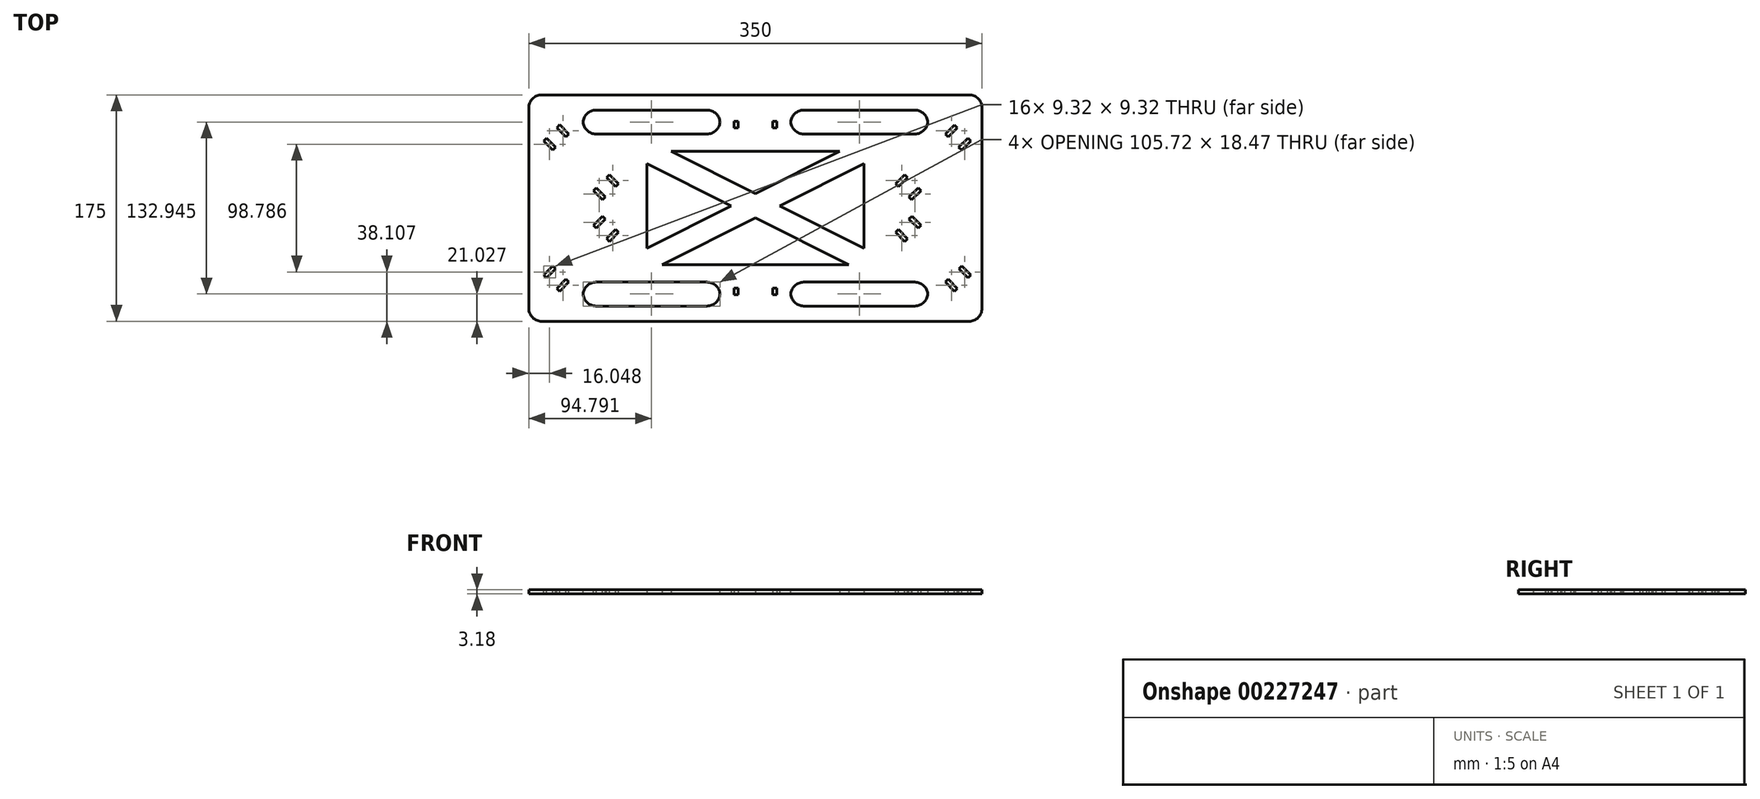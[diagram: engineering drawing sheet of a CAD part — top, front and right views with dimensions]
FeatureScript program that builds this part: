
annotation { "Feature Type Name" : "Feature", "Feature Type Description" : "" }
export const myFeature = defineFeature(function(context is Context, id is Id, definition is map)
    precondition{}
    {
        {
            var Q0;
            Q0=qCreatedBy(makeId("Top.planeOp"),FACE);
            var sketch = newSketch(context, id + "F0", { "sketchPlane" : qUnion([Q0])});
            skLineSegment(sketch, "E0.bottom", {"start": v(175, -87.5) * mm, "end": v(-175, -87.5) * mm});
            skLineSegment(sketch, "E0.top", {"start": v(175, 87.5) * mm, "end": v(-175, 87.5) * mm});
            skLineSegment(sketch, "E0.left", {"start": v(175, -87.5) * mm, "end": v(175, 87.5) * mm});
            skLineSegment(sketch, "E0.right", {"start": v(-175, -87.5) * mm, "end": v(-175, 87.5) * mm});
            skPoint(sketch, "E0.middle", {"position": v(0, 0) * mm});
            skLineSegment(sketch, "E1.bottom", {"start": v(-13.41, 62) * mm, "end": v(-16.59, 62) * mm});
            skLineSegment(sketch, "E1.top", {"start": v(-13.41, 67) * mm, "end": v(-16.59, 67) * mm});
            skLineSegment(sketch, "E1.left", {"start": v(-13.41, 62) * mm, "end": v(-13.41, 67) * mm});
            skLineSegment(sketch, "E1.right", {"start": v(-16.59, 62) * mm, "end": v(-16.59, 67) * mm});
            skPoint(sketch, "E1.middle", {"position": v(-15, 64.5) * mm});
            skLineSegment(sketch, "E2.bottom", {"start": v(13.41, 67) * mm, "end": v(16.59, 67) * mm});
            skLineSegment(sketch, "E2.top", {"start": v(13.41, 62) * mm, "end": v(16.59, 62) * mm});
            skLineSegment(sketch, "E2.left", {"start": v(13.41, 67) * mm, "end": v(13.41, 62) * mm});
            skLineSegment(sketch, "E2.right", {"start": v(16.59, 67) * mm, "end": v(16.59, 62) * mm});
            skPoint(sketch, "E3.0.1.0", {"position": v(-15, -64.5) * mm});
            skLineSegment(sketch, "E3.0.1.1", {"start": v(-16.59, -67) * mm, "end": v(-16.59, -62) * mm});
            skLineSegment(sketch, "E3.0.1.2", {"start": v(13.41, -62) * mm, "end": v(13.41, -67) * mm});
            skLineSegment(sketch, "E3.0.1.3", {"start": v(-13.41, -62) * mm, "end": v(-16.59, -62) * mm});
            skLineSegment(sketch, "E3.0.1.4", {"start": v(13.41, -67) * mm, "end": v(16.59, -67) * mm});
            skLineSegment(sketch, "E3.0.1.5", {"start": v(-13.41, -67) * mm, "end": v(-16.59, -67) * mm});
            skLineSegment(sketch, "E3.0.1.6", {"start": v(13.41, -62) * mm, "end": v(16.59, -62) * mm});
            skLineSegment(sketch, "E3.0.1.7", {"start": v(16.59, -62) * mm, "end": v(16.59, -67) * mm});
            skLineSegment(sketch, "E3.0.1.8", {"start": v(-13.41, -67) * mm, "end": v(-13.41, -62) * mm});
            skLineSegment(sketch, "E3.direction1", {"start": v(-16.59, 62) * mm, "end": v(8.41, 62) * mm, "construction": true});
            skLineSegment(sketch, "E3.direction2", {"start": v(-16.59, 62) * mm, "end": v(-16.59, -67) * mm, "construction": true});
            skSolve(sketch);
        }
        {
            var Q0;
            Q0 = qSketchRegion(id + "F0", true);
            extrude(context, id + "F1", {"entities" : qUnion([Q0]), "depth" : 3.17 * mm});
        }
        {
            var Q0;
            Q0=makeQuery(id+"F1.opExtrude","CAP_FACE",FACE,{"disambiguationData":[OSD([sQuery(id+"F0.wireOp",EDGE,"E0.bottom"),sQuery(id+"F0.wireOp",EDGE,"E0.top"),sQuery(id+"F0.wireOp",EDGE,"E0.left"),sQuery(id+"F0.wireOp",EDGE,"E0.right"),sQuery(id+"F0.wireOp",EDGE,"E1.bottom"),sQuery(id+"F0.wireOp",EDGE,"E1.top"),sQuery(id+"F0.wireOp",EDGE,"E1.left"),sQuery(id+"F0.wireOp",EDGE,"E1.right"),sQuery(id+"F0.wireOp",EDGE,"E2.bottom"),sQuery(id+"F0.wireOp",EDGE,"E2.top"),sQuery(id+"F0.wireOp",EDGE,"E2.left"),sQuery(id+"F0.wireOp",EDGE,"E2.right"),sQuery(id+"F0.wireOp",EDGE,"E3.0.1.1"),sQuery(id+"F0.wireOp",EDGE,"E3.0.1.2"),sQuery(id+"F0.wireOp",EDGE,"E3.0.1.3"),sQuery(id+"F0.wireOp",EDGE,"E3.0.1.4"),sQuery(id+"F0.wireOp",EDGE,"E3.0.1.5"),sQuery(id+"F0.wireOp",EDGE,"E3.0.1.6"),sQuery(id+"F0.wireOp",EDGE,"E3.0.1.7"),sQuery(id+"F0.wireOp",EDGE,"E3.0.1.8")])],"isStart":false});
            var sketch = newSketch(context, id + "F2", { "sketchPlane" : qUnion([Q0])});
            skLineSegment(sketch, "E4", {"start": v(-163.61, -51.8) * mm, "end": v(-156.54, -44.74) * mm});
            skLineSegment(sketch, "E5", {"start": v(-156.54, -44.74) * mm, "end": v(-154.3, -46.98) * mm});
            skLineSegment(sketch, "E6", {"start": v(-154.3, -46.98) * mm, "end": v(-161.36, -54.05) * mm});
            skLineSegment(sketch, "E7", {"start": v(-161.36, -54.05) * mm, "end": v(-163.61, -51.8) * mm});
            skLineSegment(sketch, "E8", {"start": v(-153.35, -62.06) * mm, "end": v(-146.28, -55) * mm});
            skLineSegment(sketch, "E9", {"start": v(-146.28, -55) * mm, "end": v(-144.04, -57.24) * mm});
            skLineSegment(sketch, "E10", {"start": v(-144.04, -57.24) * mm, "end": v(-151.1, -64.3) * mm});
            skLineSegment(sketch, "E11", {"start": v(-151.1, -64.3) * mm, "end": v(-153.35, -62.06) * mm});
            skLineSegment(sketch, "E12", {"start": v(166.32, 51.8) * mm, "end": v(164.07, 54.05) * mm});
            skLineSegment(sketch, "E13", {"start": v(164.07, 54.05) * mm, "end": v(157, 46.98) * mm});
            skLineSegment(sketch, "E14", {"start": v(157, 46.98) * mm, "end": v(159.24, 44.74) * mm});
            skLineSegment(sketch, "E15", {"start": v(159.24, 44.74) * mm, "end": v(166.32, 51.8) * mm});
            skLineSegment(sketch, "E16", {"start": v(156.06, 62.06) * mm, "end": v(153.81, 64.3) * mm});
            skLineSegment(sketch, "E17", {"start": v(153.81, 64.3) * mm, "end": v(146.74, 57.24) * mm});
            skLineSegment(sketch, "E18", {"start": v(146.74, 57.24) * mm, "end": v(148.99, 55) * mm});
            skLineSegment(sketch, "E19", {"start": v(148.99, 55) * mm, "end": v(156.06, 62.06) * mm});
            skLineSegment(sketch, "E20", {"start": v(-163.61, 51.8) * mm, "end": v(-161.36, 54.05) * mm});
            skLineSegment(sketch, "E21", {"start": v(-161.36, 54.05) * mm, "end": v(-154.3, 46.98) * mm});
            skLineSegment(sketch, "E22", {"start": v(-154.3, 46.98) * mm, "end": v(-156.54, 44.74) * mm});
            skLineSegment(sketch, "E23", {"start": v(-156.54, 44.74) * mm, "end": v(-163.61, 51.8) * mm});
            skLineSegment(sketch, "E24", {"start": v(-153.32, 62.1) * mm, "end": v(-151.07, 64.34) * mm});
            skLineSegment(sketch, "E25", {"start": v(-151.07, 64.34) * mm, "end": v(-144, 57.27) * mm});
            skLineSegment(sketch, "E26", {"start": v(-144, 57.27) * mm, "end": v(-146.25, 55.03) * mm});
            skLineSegment(sketch, "E27", {"start": v(-146.25, 55.03) * mm, "end": v(-153.32, 62.1) * mm});
            skLineSegment(sketch, "E28", {"start": v(164.12, -54.04) * mm, "end": v(166.37, -51.8) * mm});
            skLineSegment(sketch, "E29", {"start": v(166.37, -51.8) * mm, "end": v(159.3, -44.72) * mm});
            skLineSegment(sketch, "E30", {"start": v(159.3, -44.72) * mm, "end": v(157.05, -46.97) * mm});
            skLineSegment(sketch, "E31", {"start": v(157.05, -46.97) * mm, "end": v(164.12, -54.04) * mm});
            skLineSegment(sketch, "E32", {"start": v(153.83, -64.33) * mm, "end": v(156.07, -62.09) * mm});
            skLineSegment(sketch, "E33", {"start": v(156.07, -62.09) * mm, "end": v(149, -55.02) * mm});
            skLineSegment(sketch, "E34", {"start": v(149, -55.02) * mm, "end": v(146.76, -57.26) * mm});
            skLineSegment(sketch, "E35", {"start": v(146.76, -57.26) * mm, "end": v(153.83, -64.33) * mm});
            skLineSegment(sketch, "E36", {"start": v(125.65, -15.57) * mm, "end": v(127.9, -13.33) * mm});
            skLineSegment(sketch, "E37", {"start": v(127.9, -13.33) * mm, "end": v(120.83, -6.26) * mm});
            skLineSegment(sketch, "E38", {"start": v(120.83, -6.26) * mm, "end": v(118.58, -8.5) * mm});
            skLineSegment(sketch, "E39", {"start": v(118.58, -8.5) * mm, "end": v(125.65, -15.57) * mm});
            skLineSegment(sketch, "E40", {"start": v(115.36, -25.86) * mm, "end": v(117.6, -23.62) * mm});
            skLineSegment(sketch, "E41", {"start": v(117.6, -23.62) * mm, "end": v(110.54, -16.55) * mm});
            skLineSegment(sketch, "E42", {"start": v(110.54, -16.55) * mm, "end": v(108.3, -18.8) * mm});
            skLineSegment(sketch, "E43", {"start": v(108.3, -18.8) * mm, "end": v(115.36, -25.86) * mm});
            skLineSegment(sketch, "E44", {"start": v(127.85, 13.34) * mm, "end": v(125.6, 15.58) * mm});
            skLineSegment(sketch, "E45", {"start": v(125.6, 15.58) * mm, "end": v(118.53, 8.51) * mm});
            skLineSegment(sketch, "E46", {"start": v(118.53, 8.51) * mm, "end": v(120.78, 6.27) * mm});
            skLineSegment(sketch, "E47", {"start": v(120.78, 6.27) * mm, "end": v(127.85, 13.34) * mm});
            skLineSegment(sketch, "E48", {"start": v(117.6, 23.6) * mm, "end": v(115.35, 25.84) * mm});
            skLineSegment(sketch, "E49", {"start": v(115.35, 25.84) * mm, "end": v(108.28, 18.77) * mm});
            skLineSegment(sketch, "E50", {"start": v(108.28, 18.77) * mm, "end": v(110.52, 16.52) * mm});
            skLineSegment(sketch, "E51", {"start": v(110.52, 16.52) * mm, "end": v(117.6, 23.6) * mm});
            skLineSegment(sketch, "E52", {"start": v(-125.14, 13.34) * mm, "end": v(-122.9, 15.58) * mm});
            skLineSegment(sketch, "E53", {"start": v(-122.9, 15.58) * mm, "end": v(-115.83, 8.51) * mm});
            skLineSegment(sketch, "E54", {"start": v(-115.83, 8.51) * mm, "end": v(-118.07, 6.27) * mm});
            skLineSegment(sketch, "E55", {"start": v(-118.07, 6.27) * mm, "end": v(-125.14, 13.34) * mm});
            skLineSegment(sketch, "E56", {"start": v(-114.85, 23.63) * mm, "end": v(-112.6, 25.88) * mm});
            skLineSegment(sketch, "E57", {"start": v(-112.6, 25.88) * mm, "end": v(-105.54, 18.8) * mm});
            skLineSegment(sketch, "E58", {"start": v(-105.54, 18.8) * mm, "end": v(-107.78, 16.56) * mm});
            skLineSegment(sketch, "E59", {"start": v(-107.78, 16.56) * mm, "end": v(-114.85, 23.63) * mm});
            skLineSegment(sketch, "E60", {"start": v(-125.14, -13.34) * mm, "end": v(-118.07, -6.27) * mm});
            skLineSegment(sketch, "E61", {"start": v(-118.07, -6.27) * mm, "end": v(-115.83, -8.51) * mm});
            skLineSegment(sketch, "E62", {"start": v(-115.83, -8.51) * mm, "end": v(-122.9, -15.58) * mm});
            skLineSegment(sketch, "E63", {"start": v(-122.9, -15.58) * mm, "end": v(-125.14, -13.34) * mm});
            skLineSegment(sketch, "E64", {"start": v(-114.89, -23.6) * mm, "end": v(-107.82, -16.52) * mm});
            skLineSegment(sketch, "E65", {"start": v(-107.82, -16.52) * mm, "end": v(-105.57, -18.77) * mm});
            skLineSegment(sketch, "E66", {"start": v(-105.57, -18.77) * mm, "end": v(-112.64, -25.84) * mm});
            skLineSegment(sketch, "E67", {"start": v(-112.64, -25.84) * mm, "end": v(-114.89, -23.6) * mm});
            skSolve(sketch);
        }
        {
            var Q0;
            Q0 = qSketchRegion(id + "F2", true);
            extrude(context, id + "F3", {"entities" : qUnion([Q0]), "operationType" : NewBodyOperationType.REMOVE, "oppositeDirection" : true, "depth" : 25 * mm});
        }
        {
            var Q0;
            Q0=makeQuery(id+"F1.opExtrude","CAP_FACE",FACE,{"disambiguationData":[OSD([sQuery(id+"F0.wireOp",EDGE,"E0.bottom"),sQuery(id+"F0.wireOp",EDGE,"E0.top"),sQuery(id+"F0.wireOp",EDGE,"E0.left"),sQuery(id+"F0.wireOp",EDGE,"E0.right"),sQuery(id+"F0.wireOp",EDGE,"E1.bottom"),sQuery(id+"F0.wireOp",EDGE,"E1.top"),sQuery(id+"F0.wireOp",EDGE,"E1.left"),sQuery(id+"F0.wireOp",EDGE,"E1.right"),sQuery(id+"F0.wireOp",EDGE,"E2.bottom"),sQuery(id+"F0.wireOp",EDGE,"E2.top"),sQuery(id+"F0.wireOp",EDGE,"E2.left"),sQuery(id+"F0.wireOp",EDGE,"E2.right"),sQuery(id+"F0.wireOp",EDGE,"E3.0.1.1"),sQuery(id+"F0.wireOp",EDGE,"E3.0.1.2"),sQuery(id+"F0.wireOp",EDGE,"E3.0.1.3"),sQuery(id+"F0.wireOp",EDGE,"E3.0.1.4"),sQuery(id+"F0.wireOp",EDGE,"E3.0.1.5"),sQuery(id+"F0.wireOp",EDGE,"E3.0.1.6"),sQuery(id+"F0.wireOp",EDGE,"E3.0.1.7"),sQuery(id+"F0.wireOp",EDGE,"E3.0.1.8")])],"isStart":false});
            var sketch = newSketch(context, id + "F4", { "sketchPlane" : qUnion([Q0])});
            skLineSegment(sketch, "E68.bottom", {"start": v(138.9, -44.1) * mm, "end": v(-138.9, -44.1) * mm});
            skLineSegment(sketch, "E68.top", {"start": v(138.9, 44.1) * mm, "end": v(-138.9, 44.1) * mm});
            skLineSegment(sketch, "E68.left", {"start": v(138.9, -44.1) * mm, "end": v(138.9, 44.1) * mm});
            skLineSegment(sketch, "E68.right", {"start": v(-138.9, -44.1) * mm, "end": v(-138.9, 44.1) * mm});
            skPoint(sketch, "E68.middle", {"position": v(0, 0) * mm});
            skLineSegment(sketch, "E69", {"start": v(-138.9, 33.15) * mm, "end": v(124.66, -44.1) * mm});
            skLineSegment(sketch, "E70", {"start": v(-127.9, 44.1) * mm, "end": v(138.9, -34.1) * mm});
            skLineSegment(sketch, "E71.MirrorCS", {"start": v(127.9, 44.1) * mm, "end": v(-138.9, -34.1) * mm});
            skLineSegment(sketch, "E72.MirrorCS", {"start": v(138.9, 33.15) * mm, "end": v(-124.66, -44.1) * mm});
            skLineSegment(sketch, "E73.bottom", {"start": v(-133.1, -57.24) * mm, "end": v(-27.32, -57.24) * mm});
            skLineSegment(sketch, "E73.top", {"start": v(-133.1, -75.7) * mm, "end": v(-27.32, -75.7) * mm});
            skLineSegment(sketch, "E73.left", {"start": v(-133.1, -57.24) * mm, "end": v(-133.1, -75.7) * mm});
            skLineSegment(sketch, "E73.right", {"start": v(-27.32, -57.24) * mm, "end": v(-27.32, -75.7) * mm});
            skLineSegment(sketch, "E74.MirrorCS", {"start": v(27.32, -57.24) * mm, "end": v(27.32, -75.7) * mm});
            skLineSegment(sketch, "E75.MirrorCS", {"start": v(133.1, -57.24) * mm, "end": v(27.32, -57.24) * mm});
            skLineSegment(sketch, "E76.MirrorCS", {"start": v(133.1, -57.24) * mm, "end": v(133.1, -75.7) * mm});
            skLineSegment(sketch, "E77.MirrorCS", {"start": v(133.1, -75.7) * mm, "end": v(27.32, -75.7) * mm});
            skLineSegment(sketch, "E78.MirrorCS", {"start": v(133.1, 75.7) * mm, "end": v(27.32, 75.7) * mm});
            skLineSegment(sketch, "E79.MirrorCS", {"start": v(-133.1, 57.24) * mm, "end": v(-27.32, 57.24) * mm});
            skLineSegment(sketch, "E80.MirrorCS", {"start": v(-133.1, 75.7) * mm, "end": v(-27.32, 75.7) * mm});
            skLineSegment(sketch, "E81.MirrorCS", {"start": v(-133.1, 57.24) * mm, "end": v(-133.1, 75.7) * mm});
            skLineSegment(sketch, "E82.MirrorCS", {"start": v(-27.32, 57.24) * mm, "end": v(-27.32, 75.7) * mm});
            skLineSegment(sketch, "E83.MirrorCS", {"start": v(133.1, 57.24) * mm, "end": v(27.32, 57.24) * mm});
            skLineSegment(sketch, "E84.MirrorCS", {"start": v(133.1, 57.24) * mm, "end": v(133.1, 75.7) * mm});
            skLineSegment(sketch, "E85.MirrorCS", {"start": v(27.32, 57.24) * mm, "end": v(27.32, 75.7) * mm});
            skSolve(sketch);
        }
        {
            var Q0;
            Q0=makeQuery(id+"F4.imprint","IMPRINT",FACE,{"disambiguationData":[TD([[makeQuery(id+"F4.imprint","IMPRINT",EDGE,{"derivedFrom":sQuery(id+"F4.wireOp",EDGE,"E79.MirrorCS")}),1.0]])]});
            var Q1;
            Q1=makeQuery(id+"F4.imprint","IMPRINT",FACE,{"disambiguationData":[TD([[makeQuery(id+"F4.imprint","IMPRINT",EDGE,{"derivedFrom":sQuery(id+"F4.wireOp",EDGE,"E73.bottom")}),-1.0]])]});
            var Q2;
            Q2=makeQuery(id+"F4.imprint","IMPRINT",FACE,{"disambiguationData":[TD([[makeQuery(id+"F4.imprint","IMPRINT",EDGE,{"derivedFrom":sQuery(id+"F4.wireOp",EDGE,"E74.MirrorCS")}),1.0]])]});
            var Q3;
            Q3=makeQuery(id+"F4.imprint","IMPRINT",FACE,{"disambiguationData":[TD([[makeQuery(id+"F4.imprint","IMPRINT",EDGE,{"derivedFrom":sQuery(id+"F4.wireOp",EDGE,"E78.MirrorCS")}),1.0]])]});
            extrude(context, id + "F5", {"entities" : qUnion([Q0, Q1, Q2, Q3]), "operationType" : NewBodyOperationType.REMOVE, "oppositeDirection" : true, "depth" : 25 * mm});
        }
        {
            var Q0;
            Q0=makeQuery(id+"F1.opExtrude","SWEPT_EDGE",EDGE,{"disambiguationData":[OSD([sQuery(id+"F0.wireOp",EDGE,"E0.top"),sQuery(id+"F0.wireOp",EDGE,"E0.right")])]});
            var Q1;
            Q1=makeQuery(id+"F1.opExtrude","SWEPT_EDGE",EDGE,{"disambiguationData":[OSD([sQuery(id+"F0.wireOp",EDGE,"E0.top"),sQuery(id+"F0.wireOp",EDGE,"E0.left")])]});
            var Q2;
            Q2=makeQuery(id+"F1.opExtrude","SWEPT_EDGE",EDGE,{"disambiguationData":[OSD([sQuery(id+"F0.wireOp",EDGE,"E0.bottom"),sQuery(id+"F0.wireOp",EDGE,"E0.left")])]});
            var Q3;
            Q3=makeQuery(id+"F1.opExtrude","SWEPT_EDGE",EDGE,{"disambiguationData":[OSD([sQuery(id+"F0.wireOp",EDGE,"E0.bottom"),sQuery(id+"F0.wireOp",EDGE,"E0.right")])]});
            var Q4;
            Q4=makeQuery(id+"F5.boolean.opBoolean","COPY",EDGE,{"derivedFrom":makeQuery(id+"F5.opExtrude","SWEPT_EDGE",EDGE,{"disambiguationData":[OSD([sQuery(id+"F4.wireOp",EDGE,"E73.top"),sQuery(id+"F4.wireOp",EDGE,"E73.left")])]})});
            var Q5;
            Q5=makeQuery(id+"F5.boolean.opBoolean","COPY",EDGE,{"derivedFrom":makeQuery(id+"F5.opExtrude","SWEPT_EDGE",EDGE,{"disambiguationData":[OSD([sQuery(id+"F4.wireOp",EDGE,"E73.bottom"),sQuery(id+"F4.wireOp",EDGE,"E73.left")])]})});
            var Q6;
            Q6=makeQuery(id+"F5.boolean.opBoolean","COPY",EDGE,{"derivedFrom":makeQuery(id+"F5.opExtrude","SWEPT_EDGE",EDGE,{"disambiguationData":[OSD([sQuery(id+"F4.wireOp",EDGE,"E73.bottom"),sQuery(id+"F4.wireOp",EDGE,"E73.right")])]})});
            var Q7;
            Q7=makeQuery(id+"F5.boolean.opBoolean","COPY",EDGE,{"derivedFrom":makeQuery(id+"F5.opExtrude","SWEPT_EDGE",EDGE,{"disambiguationData":[OSD([sQuery(id+"F4.wireOp",EDGE,"E73.top"),sQuery(id+"F4.wireOp",EDGE,"E73.right")])]})});
            var Q8;
            Q8=makeQuery(id+"F5.boolean.opBoolean","COPY",EDGE,{"derivedFrom":makeQuery(id+"F5.opExtrude","SWEPT_EDGE",EDGE,{"disambiguationData":[OSD([sQuery(id+"F4.wireOp",EDGE,"E75.MirrorCS"),sQuery(id+"F4.wireOp",EDGE,"E76.MirrorCS")])]})});
            var Q9;
            Q9=makeQuery(id+"F5.boolean.opBoolean","COPY",EDGE,{"derivedFrom":makeQuery(id+"F5.opExtrude","SWEPT_EDGE",EDGE,{"disambiguationData":[OSD([sQuery(id+"F4.wireOp",EDGE,"E76.MirrorCS"),sQuery(id+"F4.wireOp",EDGE,"E77.MirrorCS")])]})});
            var Q10;
            Q10=makeQuery(id+"F5.boolean.opBoolean","COPY",EDGE,{"derivedFrom":makeQuery(id+"F5.opExtrude","SWEPT_EDGE",EDGE,{"disambiguationData":[OSD([sQuery(id+"F4.wireOp",EDGE,"E74.MirrorCS"),sQuery(id+"F4.wireOp",EDGE,"E75.MirrorCS")])]})});
            var Q11;
            Q11=makeQuery(id+"F5.boolean.opBoolean","COPY",EDGE,{"derivedFrom":makeQuery(id+"F5.opExtrude","SWEPT_EDGE",EDGE,{"disambiguationData":[OSD([sQuery(id+"F4.wireOp",EDGE,"E74.MirrorCS"),sQuery(id+"F4.wireOp",EDGE,"E77.MirrorCS")])]})});
            var Q12;
            Q12=makeQuery(id+"F5.boolean.opBoolean","COPY",EDGE,{"derivedFrom":makeQuery(id+"F5.opExtrude","SWEPT_EDGE",EDGE,{"disambiguationData":[OSD([sQuery(id+"F4.wireOp",EDGE,"E78.MirrorCS"),sQuery(id+"F4.wireOp",EDGE,"E84.MirrorCS")])]})});
            var Q13;
            Q13=makeQuery(id+"F5.boolean.opBoolean","COPY",EDGE,{"derivedFrom":makeQuery(id+"F5.opExtrude","SWEPT_EDGE",EDGE,{"disambiguationData":[OSD([sQuery(id+"F4.wireOp",EDGE,"E83.MirrorCS"),sQuery(id+"F4.wireOp",EDGE,"E84.MirrorCS")])]})});
            var Q14;
            Q14=makeQuery(id+"F5.boolean.opBoolean","COPY",EDGE,{"derivedFrom":makeQuery(id+"F5.opExtrude","SWEPT_EDGE",EDGE,{"disambiguationData":[OSD([sQuery(id+"F4.wireOp",EDGE,"E78.MirrorCS"),sQuery(id+"F4.wireOp",EDGE,"E85.MirrorCS")])]})});
            var Q15;
            Q15=makeQuery(id+"F5.boolean.opBoolean","COPY",EDGE,{"derivedFrom":makeQuery(id+"F5.opExtrude","SWEPT_EDGE",EDGE,{"disambiguationData":[OSD([sQuery(id+"F4.wireOp",EDGE,"E83.MirrorCS"),sQuery(id+"F4.wireOp",EDGE,"E85.MirrorCS")])]})});
            var Q16;
            Q16=makeQuery(id+"F5.boolean.opBoolean","COPY",EDGE,{"derivedFrom":makeQuery(id+"F5.opExtrude","SWEPT_EDGE",EDGE,{"disambiguationData":[OSD([sQuery(id+"F4.wireOp",EDGE,"E80.MirrorCS"),sQuery(id+"F4.wireOp",EDGE,"E82.MirrorCS")])]})});
            var Q17;
            Q17=makeQuery(id+"F5.boolean.opBoolean","COPY",EDGE,{"derivedFrom":makeQuery(id+"F5.opExtrude","SWEPT_EDGE",EDGE,{"disambiguationData":[OSD([sQuery(id+"F4.wireOp",EDGE,"E79.MirrorCS"),sQuery(id+"F4.wireOp",EDGE,"E82.MirrorCS")])]})});
            var Q18;
            Q18=makeQuery(id+"F5.boolean.opBoolean","COPY",EDGE,{"derivedFrom":makeQuery(id+"F5.opExtrude","SWEPT_EDGE",EDGE,{"disambiguationData":[OSD([sQuery(id+"F4.wireOp",EDGE,"E79.MirrorCS"),sQuery(id+"F4.wireOp",EDGE,"E81.MirrorCS")])]})});
            var Q19;
            Q19=makeQuery(id+"F5.boolean.opBoolean","COPY",EDGE,{"derivedFrom":makeQuery(id+"F5.opExtrude","SWEPT_EDGE",EDGE,{"disambiguationData":[OSD([sQuery(id+"F4.wireOp",EDGE,"E80.MirrorCS"),sQuery(id+"F4.wireOp",EDGE,"E81.MirrorCS")])]})});
            fillet(context, id + "F6", {"entities" : qUnion([Q0, Q1, Q2, Q3, Q4, Q5, Q6, Q7, Q8, Q9, Q10, Q11, Q12, Q13, Q14, Q15, Q16, Q17, Q18, Q19]), "radius" : 10 * mm, "tangentPropagation" : true, "allowEdgeOverflow" : false});
        }
        {
            var Q0;
            Q0=makeQuery(id+"F1.opExtrude","CAP_FACE",FACE,{"disambiguationData":[OSD([sQuery(id+"F0.wireOp",EDGE,"E0.bottom"),sQuery(id+"F0.wireOp",EDGE,"E0.top"),sQuery(id+"F0.wireOp",EDGE,"E0.left"),sQuery(id+"F0.wireOp",EDGE,"E0.right"),sQuery(id+"F0.wireOp",EDGE,"E1.bottom"),sQuery(id+"F0.wireOp",EDGE,"E1.top"),sQuery(id+"F0.wireOp",EDGE,"E1.left"),sQuery(id+"F0.wireOp",EDGE,"E1.right"),sQuery(id+"F0.wireOp",EDGE,"E2.bottom"),sQuery(id+"F0.wireOp",EDGE,"E2.top"),sQuery(id+"F0.wireOp",EDGE,"E2.left"),sQuery(id+"F0.wireOp",EDGE,"E2.right"),sQuery(id+"F0.wireOp",EDGE,"E3.0.1.1"),sQuery(id+"F0.wireOp",EDGE,"E3.0.1.2"),sQuery(id+"F0.wireOp",EDGE,"E3.0.1.3"),sQuery(id+"F0.wireOp",EDGE,"E3.0.1.4"),sQuery(id+"F0.wireOp",EDGE,"E3.0.1.5"),sQuery(id+"F0.wireOp",EDGE,"E3.0.1.6"),sQuery(id+"F0.wireOp",EDGE,"E3.0.1.7"),sQuery(id+"F0.wireOp",EDGE,"E3.0.1.8")])],"isStart":true});
            var sketch = newSketch(context, id + "F7", { "sketchPlane" : qUnion([Q0])});
            skLineSegment(sketch, "E86.bottom", {"start": v(-83.76, 43.92) * mm, "end": v(83.76, 43.92) * mm});
            skLineSegment(sketch, "E86.top", {"start": v(-83.76, -43.92) * mm, "end": v(83.76, -43.92) * mm});
            skLineSegment(sketch, "E86.left", {"start": v(-83.76, 43.92) * mm, "end": v(-83.76, -43.92) * mm});
            skLineSegment(sketch, "E86.right", {"start": v(83.76, 43.92) * mm, "end": v(83.76, -43.92) * mm});
            skPoint(sketch, "E86.middle", {"position": v(0, 0) * mm});
            skLineSegment(sketch, "E87", {"start": v(83.76, -34.4) * mm, "end": v(-71.98, 43.92) * mm});
            skLineSegment(sketch, "E88", {"start": v(65.2, -43.92) * mm, "end": v(-83.76, 31) * mm});
            skLineSegment(sketch, "E89.MirrorCS", {"start": v(-65.2, -43.92) * mm, "end": v(83.76, 31) * mm});
            skLineSegment(sketch, "E90.MirrorCS", {"start": v(-83.76, -34.4) * mm, "end": v(71.98, 43.92) * mm});
            skSolve(sketch);
        }
        {
            var Q0;
            {var subQ0=sQuery(id+"F7.wireOp",EDGE,"E87");var subQ1=sQuery(id+"F7.wireOp",EDGE,"E86.right");var subQ2=makeQuery(id+"F7.imprint","INTERSECT",VERTEX,{"derivedFrom":[subQ1,subQ0]});Q0=makeQuery(id+"F7.imprint","IMPRINT",FACE,{"disambiguationData":[TD([[makeQuery(id+"F7.imprint","IMPRINT",EDGE,{"disambiguationData":[TD([[subQ2,1.0]])],"derivedFrom":subQ1}),-1.0]])]});}
            var Q1;
            {var subQ0=sQuery(id+"F7.wireOp",EDGE,"E88");var subQ1=sQuery(id+"F7.wireOp",EDGE,"E86.top");var subQ2=makeQuery(id+"F7.imprint","INTERSECT",VERTEX,{"derivedFrom":[subQ1,subQ0]});Q1=makeQuery(id+"F7.imprint","IMPRINT",FACE,{"disambiguationData":[TD([[makeQuery(id+"F7.imprint","IMPRINT",EDGE,{"disambiguationData":[TD([[subQ2,1.0]])],"derivedFrom":subQ1}),1.0]])]});}
            var Q2;
            {var subQ0=sQuery(id+"F7.wireOp",EDGE,"E88");var subQ1=sQuery(id+"F7.wireOp",EDGE,"E86.left");var subQ2=makeQuery(id+"F7.imprint","INTERSECT",VERTEX,{"derivedFrom":[subQ1,subQ0]});Q2=makeQuery(id+"F7.imprint","IMPRINT",FACE,{"disambiguationData":[TD([[makeQuery(id+"F7.imprint","IMPRINT",EDGE,{"disambiguationData":[TD([[subQ2,-1.0]])],"derivedFrom":subQ1}),1.0]])]});}
            var Q3;
            {var subQ0=sQuery(id+"F7.wireOp",EDGE,"E87");var subQ1=sQuery(id+"F7.wireOp",EDGE,"E86.bottom");var subQ2=makeQuery(id+"F7.imprint","INTERSECT",VERTEX,{"derivedFrom":[subQ1,subQ0]});Q3=makeQuery(id+"F7.imprint","IMPRINT",FACE,{"disambiguationData":[TD([[makeQuery(id+"F7.imprint","IMPRINT",EDGE,{"disambiguationData":[TD([[subQ2,-1.0]])],"derivedFrom":subQ1}),-1.0]])]});}
            extrude(context, id + "F8", {"entities" : qUnion([Q0, Q1, Q2, Q3]), "operationType" : NewBodyOperationType.REMOVE, "oppositeDirection" : true, "depth" : 25 * mm});
        }
    });
